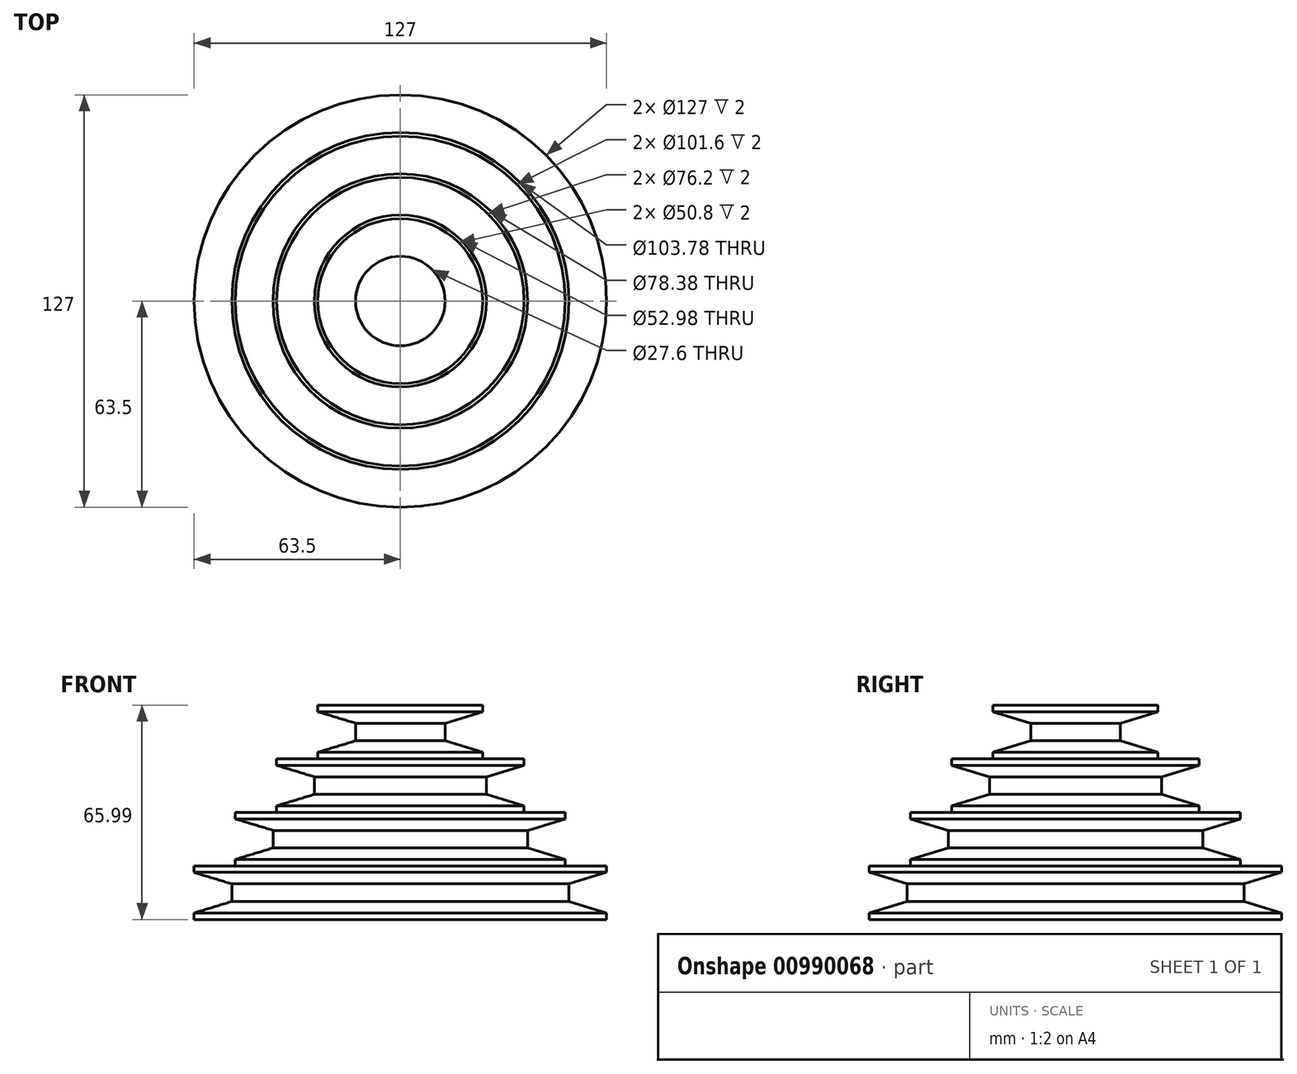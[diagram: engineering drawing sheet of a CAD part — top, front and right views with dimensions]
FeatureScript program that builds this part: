
annotation { "Feature Type Name" : "Feature", "Feature Type Description" : "" }
export const myFeature = defineFeature(function(context is Context, id is Id, definition is map)
    precondition{}
    {
        {
            var Q0;
            Q0=qCreatedBy(makeId("Front.planeOp"),FACE);
            var sketch = newSketch(context, id + "F0", { "sketchPlane" : qUnion([Q0])});
            skLineSegment(sketch, "E0", {"start": v(0, 65.99) * mm, "end": v(0, 0) * mm});
            skLineSegment(sketch, "E1", {"start": v(0, 65.99) * mm, "end": v(-25.4, 65.99) * mm});
            skLineSegment(sketch, "E2", {"start": v(-25.4, 65.99) * mm, "end": v(-25.4, 63.99) * mm});
            skLineSegment(sketch, "E3", {"start": v(-25.4, 63.99) * mm, "end": v(-13.8, 60.44) * mm});
            skLineSegment(sketch, "E4", {"start": v(-13.8, 60.44) * mm, "end": v(-13.8, 55.04) * mm});
            skLineSegment(sketch, "E5", {"start": v(-13.8, 55.04) * mm, "end": v(-25.4, 51.49) * mm});
            skLineSegment(sketch, "E6", {"start": v(-25.4, 51.49) * mm, "end": v(-25.4, 49.49) * mm});
            skLineSegment(sketch, "E7", {"start": v(-25.4, 49.49) * mm, "end": v(-38.1, 49.49) * mm});
            skLineSegment(sketch, "E8", {"start": v(-38.1, 49.49) * mm, "end": v(-38.1, 47.49) * mm});
            skLineSegment(sketch, "E9", {"start": v(-38.1, 47.49) * mm, "end": v(-26.5, 43.94) * mm});
            skLineSegment(sketch, "E10", {"start": v(-26.5, 43.94) * mm, "end": v(-26.5, 38.54) * mm});
            skLineSegment(sketch, "E11", {"start": v(-26.5, 38.54) * mm, "end": v(-38.1, 35) * mm});
            skLineSegment(sketch, "E12", {"start": v(-38.1, 35) * mm, "end": v(-38.1, 33) * mm});
            skLineSegment(sketch, "E13", {"start": v(-38.1, 33) * mm, "end": v(-50.8, 33) * mm});
            skLineSegment(sketch, "E14", {"start": v(-50.8, 33) * mm, "end": v(-50.8, 31) * mm});
            skLineSegment(sketch, "E15", {"start": v(-50.8, 31) * mm, "end": v(-39.2, 27.44) * mm});
            skLineSegment(sketch, "E16", {"start": v(-39.2, 27.44) * mm, "end": v(-39.2, 22.04) * mm});
            skLineSegment(sketch, "E17", {"start": v(-39.2, 22.04) * mm, "end": v(-50.8, 18.5) * mm});
            skLineSegment(sketch, "E18", {"start": v(-50.8, 18.5) * mm, "end": v(-50.8, 16.5) * mm});
            skLineSegment(sketch, "E19", {"start": v(-50.8, 16.5) * mm, "end": v(-63.5, 16.5) * mm});
            skLineSegment(sketch, "E20", {"start": v(-63.5, 16.5) * mm, "end": v(-63.5, 14.5) * mm});
            skLineSegment(sketch, "E21", {"start": v(-63.5, 14.5) * mm, "end": v(-51.9, 10.95) * mm});
            skLineSegment(sketch, "E22", {"start": v(-51.9, 10.95) * mm, "end": v(-51.9, 5.55) * mm});
            skLineSegment(sketch, "E23", {"start": v(-51.9, 5.55) * mm, "end": v(-63.5, 2) * mm});
            skLineSegment(sketch, "E24", {"start": v(-63.5, 2) * mm, "end": v(-63.5, 0) * mm});
            skPoint(sketch, "E25.start.orphan", {"position": v(-127, 0) * mm});
            skPoint(sketch, "E26.start.orphan", {"position": v(-127, -27.12) * mm});
            skPoint(sketch, "E27.end.orphan", {"position": v(0, -34.12) * mm});
            skPoint(sketch, "E28.end.orphan", {"position": v(-127, 57.58) * mm});
            skLineSegment(sketch, "E29", {"start": v(-63.5, 0) * mm, "end": v(0, 0) * mm});
            skSolve(sketch);
        }
        {
            var Q0;
            Q0=sQuery(id+"F0.wireOp",EDGE,"E1");
            var Q1;
            Q1=sQuery(id+"F0.wireOp",EDGE,"E2");
            var Q2;
            Q2=sQuery(id+"F0.wireOp",EDGE,"E3");
            var Q3;
            Q3=sQuery(id+"F0.wireOp",EDGE,"E4");
            var Q4;
            Q4=sQuery(id+"F0.wireOp",EDGE,"E5");
            var Q5;
            Q5=sQuery(id+"F0.wireOp",EDGE,"E6");
            var Q6;
            Q6=sQuery(id+"F0.wireOp",EDGE,"E7");
            var Q7;
            Q7=sQuery(id+"F0.wireOp",EDGE,"E8");
            var Q8;
            Q8=sQuery(id+"F0.wireOp",EDGE,"E9");
            var Q9;
            Q9=sQuery(id+"F0.wireOp",EDGE,"E10");
            var Q10;
            Q10=sQuery(id+"F0.wireOp",EDGE,"E11");
            var Q11;
            Q11=sQuery(id+"F0.wireOp",EDGE,"E12");
            var Q12;
            Q12=sQuery(id+"F0.wireOp",EDGE,"E13");
            var Q13;
            Q13=sQuery(id+"F0.wireOp",EDGE,"E14");
            var Q14;
            Q14=sQuery(id+"F0.wireOp",EDGE,"E15");
            var Q15;
            Q15=sQuery(id+"F0.wireOp",EDGE,"E16");
            var Q16;
            Q16=sQuery(id+"F0.wireOp",EDGE,"E17");
            var Q17;
            Q17=sQuery(id+"F0.wireOp",EDGE,"E18");
            var Q18;
            Q18=sQuery(id+"F0.wireOp",EDGE,"E19");
            var Q19;
            Q19=sQuery(id+"F0.wireOp",EDGE,"E20");
            var Q20;
            Q20=sQuery(id+"F0.wireOp",EDGE,"E21");
            var Q21;
            Q21=sQuery(id+"F0.wireOp",EDGE,"E22");
            var Q22;
            Q22=sQuery(id+"F0.wireOp",EDGE,"E23");
            var Q23;
            Q23=sQuery(id+"F0.wireOp",EDGE,"E24");
            var Q24;
            Q24=sQuery(id+"F0.wireOp",EDGE,"E29");
            var Q25;
            Q25=sQuery(id+"F0.wireOp",EDGE,"E0");
            revolve(context, id + "F1", {"bodyType" : ToolBodyType.SURFACE, "surfaceOperationType" : NewSurfaceOperationType.NEW, "surfaceEntities" : qUnion([Q0, Q1, Q2, Q3, Q4, Q5, Q6, Q7, Q8, Q9, Q10, Q11, Q12, Q13, Q14, Q15, Q16, Q17, Q18, Q19, Q20, Q21, Q22, Q23, Q24]), "axis" : qUnion([Q25]), "revolveType" : RevolveType.FULL});
        }
    });
